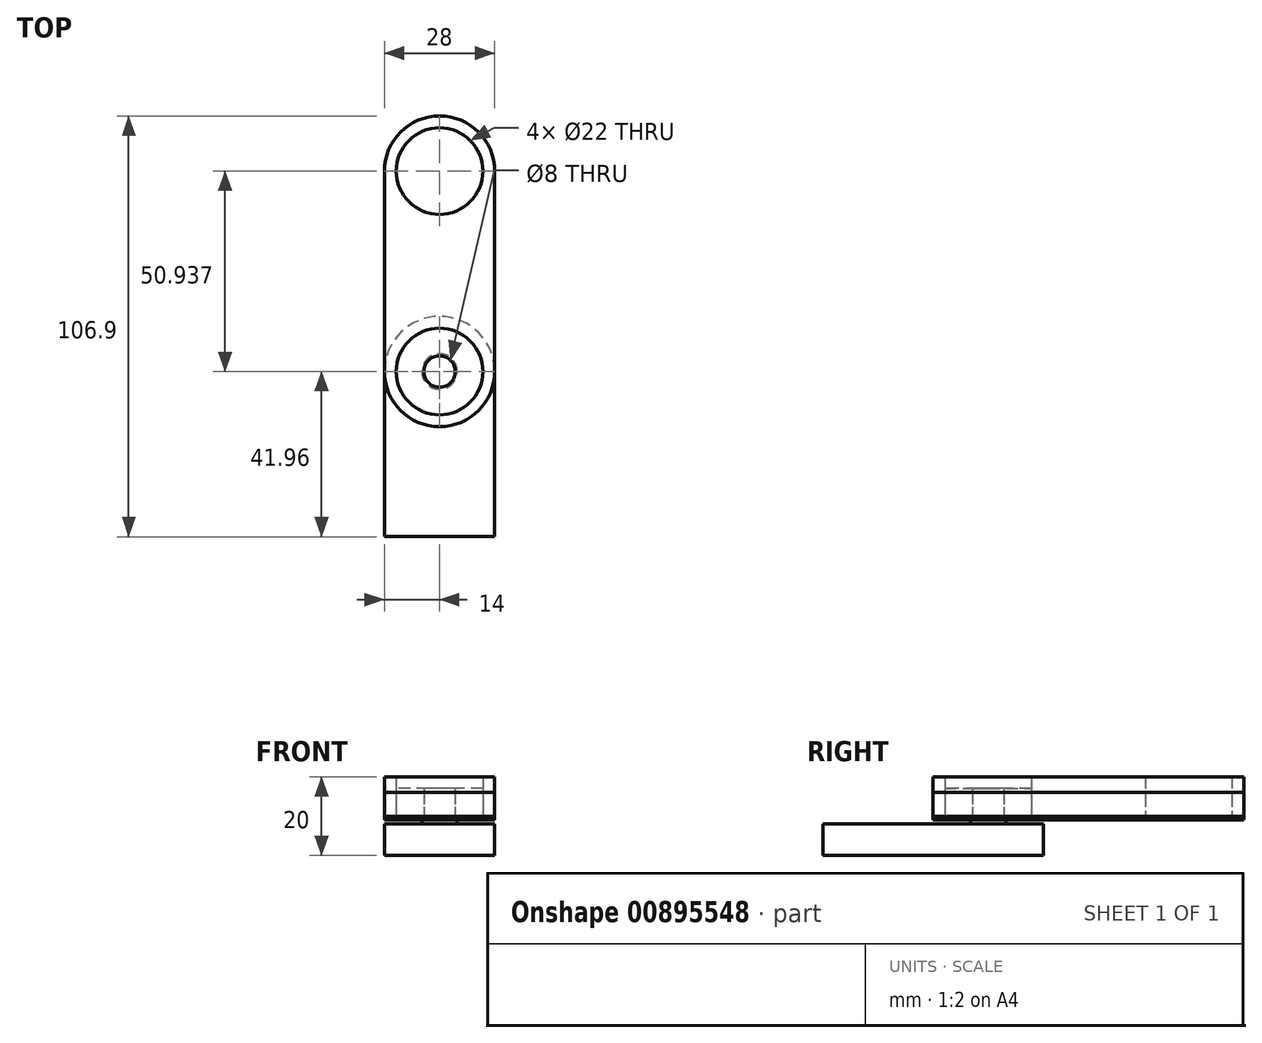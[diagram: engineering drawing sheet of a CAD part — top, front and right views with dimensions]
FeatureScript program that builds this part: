
annotation { "Feature Type Name" : "Feature", "Feature Type Description" : "" }
export const myFeature = defineFeature(function(context is Context, id is Id, definition is map)
    precondition{}
    {
        {
            var Q0;
            Q0=qCreatedBy(makeId("Top.planeOp"),FACE);
            var sketch = newSketch(context, id + "F0", { "sketchPlane" : qUnion([Q0])});
            skCircle(sketch, "E0", {"center": v(0, 0) * mm, "radius": 4 * mm});
            skCircle(sketch, "E1", {"center": v(0, 0) * mm, "radius": 11 * mm});
            skLineSegment(sketch, "E2.bottom", {"start": v(14, 0) * mm, "end": v(0, 0) * mm});
            skLineSegment(sketch, "E2.top", {"start": v(14, 50.94) * mm, "end": v(0, 50.94) * mm});
            skLineSegment(sketch, "E2.left", {"start": v(14, 0) * mm, "end": v(14, 50.94) * mm});
            skLineSegment(sketch, "E2.right", {"start": v(0, 0) * mm, "end": v(0, 50.94) * mm});
            skLineSegment(sketch, "E3.MirrorCS", {"start": v(-14, 50.94) * mm, "end": v(0, 50.94) * mm});
            skLineSegment(sketch, "E4.MirrorCS", {"start": v(-14, 0) * mm, "end": v(-14, 50.94) * mm});
            skCircle(sketch, "E5", {"center": v(0, 0) * mm, "radius": 14 * mm});
            skCircle(sketch, "E6", {"center": v(0, 50.94) * mm, "radius": 14 * mm});
            skCircle(sketch, "E7", {"center": v(0, 50.94) * mm, "radius": 11 * mm});
            skCircle(sketch, "E8", {"center": v(0, 0) * mm, "radius": 4.5 * mm});
            skSolve(sketch);
        }
        {
            var Q0;
            Q0=makeQuery(id+"F0.imprint","IMPRINT",FACE,{"disambiguationData":[TD([[makeQuery(id+"F0.imprint","IMPRINT",EDGE,{"derivedFrom":sQuery(id+"F0.wireOp",EDGE,"E0")}),-1.0]])]});
            var Q1;
            {var subQ0=sQuery(id+"F0.wireOp",EDGE,"E2.bottom");var subQ1=sQuery(id+"F0.wireOp",EDGE,"E1");var subQ2=makeQuery(id+"F0.imprint","INTERSECT",VERTEX,{"derivedFrom":[subQ1,subQ0]});Q1=makeQuery(id+"F0.imprint","IMPRINT",FACE,{"disambiguationData":[TD([[makeQuery(id+"F0.imprint","IMPRINT",EDGE,{"disambiguationData":[TD([[subQ2,-1.0]])],"derivedFrom":subQ1}),1.0]])]});}
            var Q2;
            {var subQ0=sQuery(id+"F0.wireOp",EDGE,"E2.bottom");var subQ1=sQuery(id+"F0.wireOp",EDGE,"E1");var subQ2=makeQuery(id+"F0.imprint","INTERSECT",VERTEX,{"derivedFrom":[subQ1,subQ0]});Q2=makeQuery(id+"F0.imprint","IMPRINT",FACE,{"disambiguationData":[TD([[makeQuery(id+"F0.imprint","IMPRINT",EDGE,{"disambiguationData":[TD([[subQ2,1.0]])],"derivedFrom":subQ1}),1.0]])]});}
            extrude(context, id + "F1", {"entities" : qUnion([Q0, Q1, Q2]), "depth" : 7 * mm, "offsetDistance" : 25 * mm});
        }
        {
            var Q0;
            {var subQ0=sQuery(id+"F0.wireOp",EDGE,"E2.bottom");var subQ1=sQuery(id+"F0.wireOp",EDGE,"E1");var subQ2=makeQuery(id+"F0.imprint","INTERSECT",VERTEX,{"derivedFrom":[subQ1,subQ0]});Q0=makeQuery(id+"F0.imprint","IMPRINT",FACE,{"disambiguationData":[TD([[makeQuery(id+"F0.imprint","IMPRINT",EDGE,{"disambiguationData":[TD([[subQ2,-1.0]])],"derivedFrom":subQ1}),-1.0]])]});}
            var Q1;
            {var subQ4=sQuery(id+"F0.wireOp",EDGE,"E1");var subQ6=sQuery(id+"F0.wireOp",EDGE,"E2.bottom");var subQ8=makeQuery(id+"F0.imprint","INTERSECT",VERTEX,{"derivedFrom":[subQ4,subQ6]});Q1=makeQuery(id+"F0.imprint","IMPRINT",FACE,{"disambiguationData":[TD([[makeQuery(id+"F0.imprint","IMPRINT",EDGE,{"disambiguationData":[TD([[subQ8,1.0]])],"derivedFrom":subQ4}),-1.0]])]});}
            var Q2;
            {var subQ0=sQuery(id+"F0.wireOp",EDGE,"E2.left");Q2=makeQuery(id+"F0.imprint","IMPRINT",FACE,{"disambiguationData":[TD([[makeQuery(id+"F0.imprint","IMPRINT",EDGE,{"derivedFrom":subQ0}),1.0]])]});}
            var Q3;
            {var subQ5=sQuery(id+"F0.wireOp",EDGE,"E4.MirrorCS");Q3=makeQuery(id+"F0.imprint","IMPRINT",FACE,{"disambiguationData":[TD([[makeQuery(id+"F0.imprint","IMPRINT",EDGE,{"derivedFrom":subQ5}),-1.0]])]});}
            var Q4;
            {var subQ1=sQuery(id+"F0.wireOp",EDGE,"E2.top");var subQ3=sQuery(id+"F0.wireOp",EDGE,"E7");var subQ4=makeQuery(id+"F0.imprint","INTERSECT",VERTEX,{"derivedFrom":[subQ1,subQ3]});Q4=makeQuery(id+"F0.imprint","IMPRINT",FACE,{"disambiguationData":[TD([[makeQuery(id+"F0.imprint","IMPRINT",EDGE,{"disambiguationData":[TD([[subQ4,-1.0]])],"derivedFrom":subQ3}),-1.0]])]});}
            var Q5;
            {var subQ0=sQuery(id+"F0.wireOp",EDGE,"E6");var subQ5=sQuery(id+"F0.wireOp",EDGE,"E2.right");var subQ7=makeQuery(id+"F0.imprint","INTERSECT",VERTEX,{"derivedFrom":[subQ5,subQ0]});Q5=makeQuery(id+"F0.imprint","IMPRINT",FACE,{"disambiguationData":[TD([[makeQuery(id+"F0.imprint","IMPRINT",EDGE,{"disambiguationData":[TD([[subQ7,-1.0]])],"derivedFrom":subQ5}),-1.0]])]});}
            var Q6;
            {var subQ0=sQuery(id+"F0.wireOp",EDGE,"E6");var subQ1=sQuery(id+"F0.wireOp",EDGE,"E2.right");var subQ2=makeQuery(id+"F0.imprint","INTERSECT",VERTEX,{"derivedFrom":[subQ1,subQ0]});Q6=makeQuery(id+"F0.imprint","IMPRINT",FACE,{"disambiguationData":[TD([[makeQuery(id+"F0.imprint","IMPRINT",EDGE,{"disambiguationData":[TD([[subQ2,-1.0]])],"derivedFrom":subQ1}),1.0]])]});}
            extrude(context, id + "F2", {"entities" : qUnion([Q0, Q1, Q2, Q3, Q4, Q5, Q6]), "depth" : 10 * mm, "offsetDistance" : 25 * mm});
        }
        {
            var Q0;
            {var subQ0=sQuery(id+"F0.wireOp",EDGE,"E2.bottom");var subQ1=sQuery(id+"F0.wireOp",EDGE,"E0");var subQ2=makeQuery(id+"F0.imprint","INTERSECT",VERTEX,{"derivedFrom":[subQ1,subQ0]});Q0=makeQuery(id+"F0.imprint","IMPRINT",FACE,{"disambiguationData":[TD([[makeQuery(id+"F0.imprint","IMPRINT",EDGE,{"disambiguationData":[TD([[subQ2,1.0]])],"derivedFrom":subQ1}),1.0]])]});}
            var Q1;
            {var subQ0=sQuery(id+"F0.wireOp",EDGE,"E2.bottom");var subQ1=sQuery(id+"F0.wireOp",EDGE,"E0");var subQ2=makeQuery(id+"F0.imprint","INTERSECT",VERTEX,{"derivedFrom":[subQ1,subQ0]});Q1=makeQuery(id+"F0.imprint","IMPRINT",FACE,{"disambiguationData":[TD([[makeQuery(id+"F0.imprint","IMPRINT",EDGE,{"disambiguationData":[TD([[subQ2,-1.0]])],"derivedFrom":subQ1}),1.0]])]});}
            extrude(context, id + "F3", {"entities" : qUnion([Q0, Q1]), "depth" : 6 * mm, "offsetDistance" : 25 * mm, "hasSecondDirection" : true, "secondDirectionOppositeDirection" : true, "secondDirectionDepth" : 1 * mm});
        }
        {
            var Q0;
            {var subQ0=sQuery(id+"F0.wireOp",EDGE,"E2.bottom");var subQ1=sQuery(id+"F0.wireOp",EDGE,"E0");var subQ2=makeQuery(id+"F0.imprint","INTERSECT",VERTEX,{"derivedFrom":[subQ1,subQ0]});Q0=makeQuery(id+"F0.imprint","IMPRINT",FACE,{"disambiguationData":[TD([[makeQuery(id+"F0.imprint","IMPRINT",EDGE,{"disambiguationData":[TD([[subQ2,1.0]])],"derivedFrom":subQ1}),-1.0]])]});}
            var Q1;
            {var subQ0=sQuery(id+"F0.wireOp",EDGE,"E2.bottom");var subQ1=sQuery(id+"F0.wireOp",EDGE,"E0");var subQ2=makeQuery(id+"F0.imprint","INTERSECT",VERTEX,{"derivedFrom":[subQ1,subQ0]});Q1=makeQuery(id+"F0.imprint","IMPRINT",FACE,{"disambiguationData":[TD([[makeQuery(id+"F0.imprint","IMPRINT",EDGE,{"disambiguationData":[TD([[subQ2,-1.0]])],"derivedFrom":subQ1}),-1.0]])]});}
            var Q2;
            {var subQ0=sQuery(id+"F0.wireOp",EDGE,"E2.bottom");var subQ1=sQuery(id+"F0.wireOp",EDGE,"E0");var subQ2=makeQuery(id+"F0.imprint","INTERSECT",VERTEX,{"derivedFrom":[subQ1,subQ0]});Q2=makeQuery(id+"F0.imprint","IMPRINT",FACE,{"disambiguationData":[TD([[makeQuery(id+"F0.imprint","IMPRINT",EDGE,{"disambiguationData":[TD([[subQ2,-1.0]])],"derivedFrom":subQ1}),1.0]])]});}
            var Q3;
            {var subQ0=sQuery(id+"F0.wireOp",EDGE,"E2.bottom");var subQ1=sQuery(id+"F0.wireOp",EDGE,"E0");var subQ2=makeQuery(id+"F0.imprint","INTERSECT",VERTEX,{"derivedFrom":[subQ1,subQ0]});Q3=makeQuery(id+"F0.imprint","IMPRINT",FACE,{"disambiguationData":[TD([[makeQuery(id+"F0.imprint","IMPRINT",EDGE,{"disambiguationData":[TD([[subQ2,1.0]])],"derivedFrom":subQ1}),1.0]])]});}
            extrude(context, id + "F4", {"entities" : qUnion([Q0, Q1, Q2, Q3]), "operationType" : NewBodyOperationType.ADD, "oppositeDirection" : true, "depth" : 7.2 * mm, "offsetDistance" : 25 * mm, "hasSecondDirection" : true, "secondDirectionOppositeDirection" : true, "secondDirectionDepth" : 1 * mm});
        }
        {
            var Q0;
            Q0=qCreatedBy(makeId("Top.planeOp"),FACE);
            var sketch = newSketch(context, id + "F5", { "sketchPlane" : qUnion([Q0])});
            skCircle(sketch, "E9", {"center": v(0, 0) * mm, "radius": 14 * mm});
            skLineSegment(sketch, "E10.bottom", {"start": v(14, 0) * mm, "end": v(-14, 0) * mm});
            skLineSegment(sketch, "E10.top", {"start": v(14, -41.96) * mm, "end": v(-14, -41.96) * mm});
            skLineSegment(sketch, "E10.left", {"start": v(14, 0) * mm, "end": v(14, -41.96) * mm});
            skLineSegment(sketch, "E10.right", {"start": v(-14, 0) * mm, "end": v(-14, -41.96) * mm});
            skSolve(sketch);
        }
        {
            var Q0;
            {var subQ0=sQuery(id+"F5.wireOp",EDGE,"E10.bottom");Q0=makeQuery(id+"F5.imprint","IMPRINT",FACE,{"disambiguationData":[TD([[makeQuery(id+"F5.imprint","IMPRINT",EDGE,{"derivedFrom":subQ0}),-1.0]])]});}
            var Q1;
            {var subQ0=sQuery(id+"F5.wireOp",EDGE,"E10.bottom");Q1=makeQuery(id+"F5.imprint","IMPRINT",FACE,{"disambiguationData":[TD([[makeQuery(id+"F5.imprint","IMPRINT",EDGE,{"derivedFrom":subQ0}),1.0]])]});}
            extrude(context, id + "F6", {"entities" : qUnion([Q0, Q1]), "operationType" : NewBodyOperationType.ADD, "oppositeDirection" : true, "depth" : 10 * mm, "offsetDistance" : 25 * mm, "hasSecondDirection" : true, "secondDirectionOppositeDirection" : true, "secondDirectionDepth" : 2 * mm});
        }
        {
            var Q0;
            Q0=makeQuery(id+"F5.imprint","IMPRINT",FACE,{"disambiguationData":[TD([[makeQuery(id+"F5.imprint","IMPRINT",EDGE,{"derivedFrom":sQuery(id+"F5.wireOp",EDGE,"E10.top")}),-1.0]])]});
            extrude(context, id + "F7", {"entities" : qUnion([Q0]), "operationType" : NewBodyOperationType.ADD, "oppositeDirection" : true, "depth" : 10 * mm, "offsetDistance" : 25 * mm, "hasSecondDirection" : true, "secondDirectionOppositeDirection" : true, "secondDirectionDepth" : 2 * mm});
        }
        {
            var Q0;
            {var subQ4=sQuery(id+"F0.wireOp",EDGE,"E1");var subQ6=sQuery(id+"F0.wireOp",EDGE,"E2.bottom");var subQ7=makeQuery(id+"F0.imprint","INTERSECT",VERTEX,{"derivedFrom":[subQ4,subQ6]});Q0=makeQuery(id+"F0.imprint","IMPRINT",FACE,{"disambiguationData":[TD([[makeQuery(id+"F0.imprint","IMPRINT",EDGE,{"disambiguationData":[TD([[subQ7,1.0]])],"derivedFrom":subQ4}),-1.0]])]});}
            var Q1;
            {var subQ0=sQuery(id+"F0.wireOp",EDGE,"E2.bottom");var subQ1=sQuery(id+"F0.wireOp",EDGE,"E1");var subQ2=makeQuery(id+"F0.imprint","INTERSECT",VERTEX,{"derivedFrom":[subQ1,subQ0]});Q1=makeQuery(id+"F0.imprint","IMPRINT",FACE,{"disambiguationData":[TD([[makeQuery(id+"F0.imprint","IMPRINT",EDGE,{"disambiguationData":[TD([[subQ2,-1.0]])],"derivedFrom":subQ1}),-1.0]])]});}
            var Q2;
            {var subQ0=sQuery(id+"F0.wireOp",EDGE,"E2.left");Q2=makeQuery(id+"F0.imprint","IMPRINT",FACE,{"disambiguationData":[TD([[makeQuery(id+"F0.imprint","IMPRINT",EDGE,{"derivedFrom":subQ0}),1.0]])]});}
            var Q3;
            {var subQ5=sQuery(id+"F0.wireOp",EDGE,"E4.MirrorCS");Q3=makeQuery(id+"F0.imprint","IMPRINT",FACE,{"disambiguationData":[TD([[makeQuery(id+"F0.imprint","IMPRINT",EDGE,{"derivedFrom":subQ5}),-1.0]])]});}
            var Q4;
            {var subQ0=sQuery(id+"F0.wireOp",EDGE,"E6");var subQ1=sQuery(id+"F0.wireOp",EDGE,"E2.right");var subQ2=makeQuery(id+"F0.imprint","INTERSECT",VERTEX,{"derivedFrom":[subQ1,subQ0]});Q4=makeQuery(id+"F0.imprint","IMPRINT",FACE,{"disambiguationData":[TD([[makeQuery(id+"F0.imprint","IMPRINT",EDGE,{"disambiguationData":[TD([[subQ2,-1.0]])],"derivedFrom":subQ1}),1.0]])]});}
            var Q5;
            {var subQ1=sQuery(id+"F0.wireOp",EDGE,"E2.top");var subQ3=sQuery(id+"F0.wireOp",EDGE,"E7");var subQ4=makeQuery(id+"F0.imprint","INTERSECT",VERTEX,{"derivedFrom":[subQ1,subQ3]});Q5=makeQuery(id+"F0.imprint","IMPRINT",FACE,{"disambiguationData":[TD([[makeQuery(id+"F0.imprint","IMPRINT",EDGE,{"disambiguationData":[TD([[subQ4,-1.0]])],"derivedFrom":subQ3}),-1.0]])]});}
            var Q6;
            {var subQ0=sQuery(id+"F0.wireOp",EDGE,"E6");var subQ5=sQuery(id+"F0.wireOp",EDGE,"E2.right");var subQ6=makeQuery(id+"F0.imprint","INTERSECT",VERTEX,{"derivedFrom":[subQ5,subQ0]});Q6=makeQuery(id+"F0.imprint","IMPRINT",FACE,{"disambiguationData":[TD([[makeQuery(id+"F0.imprint","IMPRINT",EDGE,{"disambiguationData":[TD([[subQ6,-1.0]])],"derivedFrom":subQ5}),-1.0]])]});}
            extrude(context, id + "F8", {"entities" : qUnion([Q0, Q1, Q2, Q3, Q4, Q5, Q6]), "depth" : 6 * mm, "offsetDistance" : 25 * mm, "hasSecondDirection" : true, "secondDirectionOppositeDirection" : true, "secondDirectionDepth" : 1 * mm});
        }
    });
